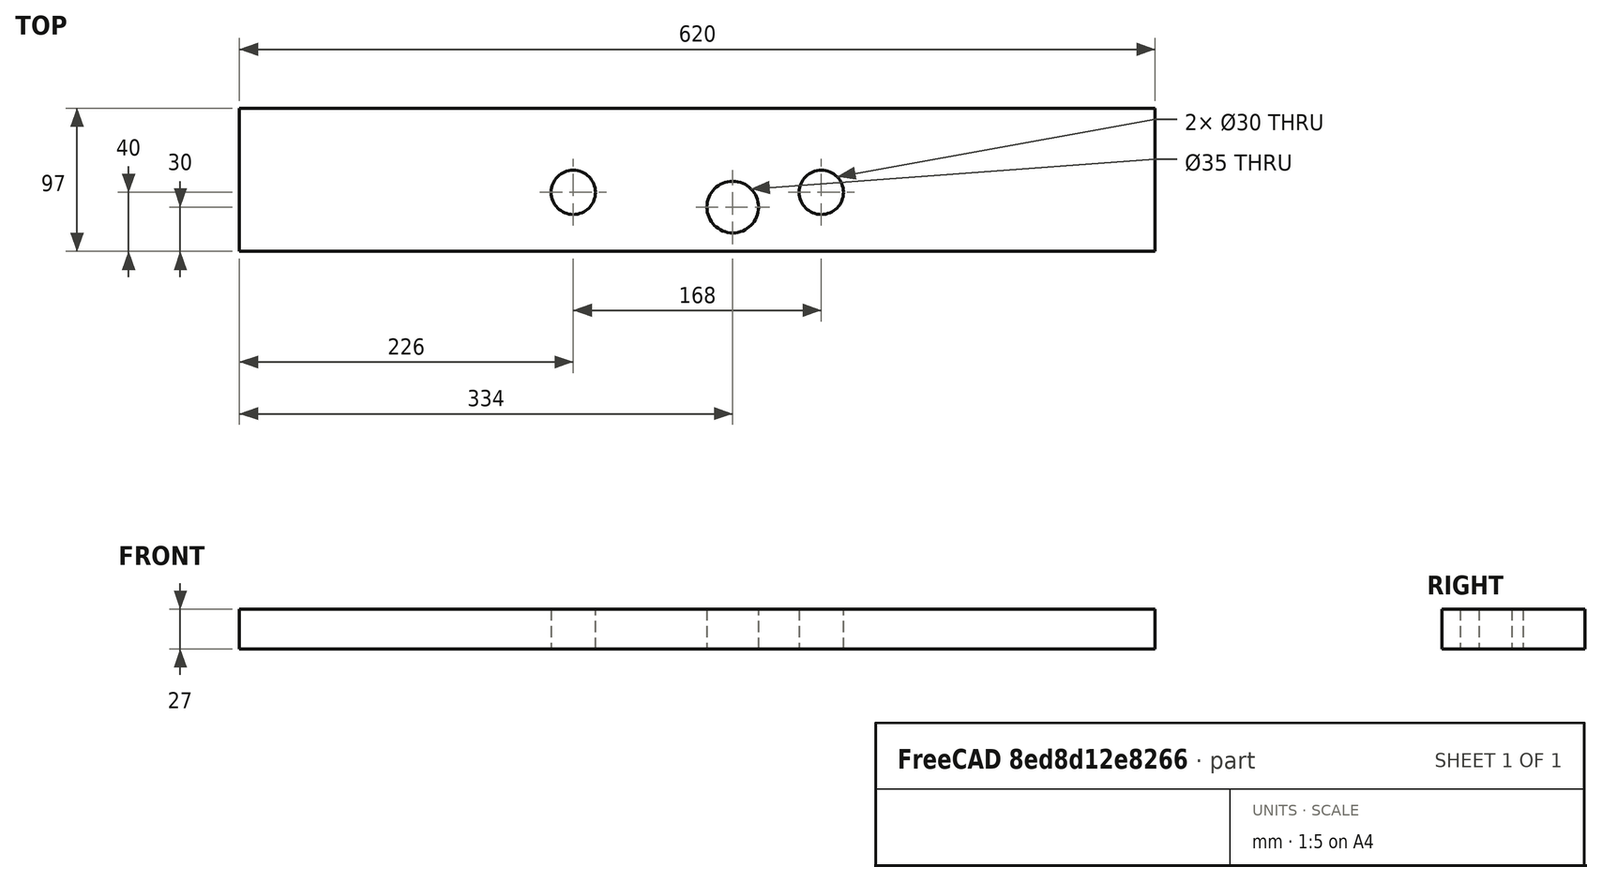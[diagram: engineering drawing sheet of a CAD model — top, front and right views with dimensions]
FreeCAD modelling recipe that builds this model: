
FCSTD DOCUMENT  (FreeCAD 0.20R25131 (Git))
Label: Zange
License: All rights reserved
LicenseURL: http://en.wikipedia.org/wiki/All_rights_reserved
objects: Part::FeaturePython×10, Part::Cylinder×3, App::FeaturePython×2, Part::Box×1, Part::MultiFuse×1, Part::Cut×1
note: 15 computed .brp shape members not serialized (recipe doc carries the construction recipe); baked Part::Feature solids carry a one-line shape summary decoded from their .brp
EXTERNAL_REF file=Grunddaten.FCStd obj=Spreadsheet

FEATURE [Part::Box] Box  label="Cube"
  AttacherType = Attacher::AttachEngine3D
  Height = 27
  Length = 620
  Placement = pos=(-310,0,0) rot=(0,0,1;0rad)
  Width = 97
  expr: .Placement.Base.x = -Length / 2
  expr: Length = <<Grunddaten>>#Spreadsheet.Arbeitsflaeche + 2 * <<Grunddaten>>#Spreadsheet.Ueberstand
  expr: Width = <<Grunddaten>>#Spreadsheet.Hoehe
  expr: Height = <<Grunddaten>>#Spreadsheet.Plattendicke
FEATURE [Part::Cylinder] Cylinder  label="Führung_rechts"
  Angle = 360
  AttacherType = Attacher::AttachEngine3D
  FirstAngle = 0
  Height = 30
  Placement = pos=(84,40,0) rot=(0,0,1;0rad)
  Radius = 15
  SecondAngle = 0
  expr: .Placement.Base.y = -Grunddaten#Spreadsheet.Plattendicke + Grunddaten#Spreadsheet.Hoehe - Grunddaten#Spreadsheet.Spindel_Hoehe
  expr: .Placement.Base.x = Grunddaten#Spreadsheet.Spindel_Links
FEATURE [Part::Cylinder] Cylinder001  label="Führung_links"
  Angle = 360
  AttacherType = Attacher::AttachEngine3D
  FirstAngle = 0
  Height = 30
  Placement = pos=(-84,40,0) rot=(0,0,1;0rad)
  Radius = 15
  SecondAngle = 0
  expr: .Placement.Base.y = -Grunddaten#Spreadsheet.Plattendicke + Grunddaten#Spreadsheet.Hoehe - Grunddaten#Spreadsheet.Spindel_Hoehe
  expr: .Placement.Base.x = -Grunddaten#Spreadsheet.Spindel_Links
FEATURE [Part::Cylinder] Cylinder002  label="Spindel"
  Angle = 360
  AttacherType = Attacher::AttachEngine3D
  FirstAngle = 0
  Height = 30
  Placement = pos=(24,30,0) rot=(0,0,1;0rad)
  Radius = 17.5
  SecondAngle = 0
  expr: .Placement.Base.x = Grunddaten#Spreadsheet.Spindel_Antrieb
  expr: .Placement.Base.y = -Grunddaten#Spreadsheet.Plattendicke + Grunddaten#Spreadsheet.Hoehe - Grunddaten#Spreadsheet.Spindel_Antrieb_Hoehe
FEATURE [App::FeaturePython] Constraints  # WARN: FeaturePython — macro-defined, semantics opaque (R4)
  _Version = 1
FEATURE [Part::MultiFuse] Fusion
  Shapes = -> [Cylinder,Cylinder001,Cylinder002]
FEATURE [Part::Cut] Cut
  Base = -> Box
  Tool = -> Fusion
FEATURE [Part::FeaturePython] Parts  # WARN: FeaturePython — macro-defined, semantics opaque (R4)
  Group = -> [Box,Cylinder,Cylinder001,Cylinder002,Fusion,Cut]
  GroupMode = 0
FEATURE [Part::FeaturePython] Assembly  label="Zange"  # WARN: FeaturePython — macro-defined, semantics opaque (R4)
  AutoRelax = true
  BuildShape = 0
  Freeze = false
  Group = -> [Constraints,Elements,Parts]
  Verbose = false
  _SolverType = 1
  _Version = 1
FEATURE [App::FeaturePython] Elements  # WARN: FeaturePython — macro-defined, semantics opaque (R4)
  Group = -> [Element,Element001,Element002,Element003,Element004,Element005,Element006,Element007]
FEATURE [Part::FeaturePython] Element  label="Vorne"  # link proxy (typed FeaturePython)
  Detach = false
  LinkTransform = true
  LinkedObject = -> Cut [Face3]
  _Parent = -> Elements
FEATURE [Part::FeaturePython] Element001  label="Oben"  # link proxy (typed FeaturePython)
  Detach = false
  LinkTransform = true
  LinkedObject = -> Cut [Face4]
  _Parent = -> Elements
FEATURE [Part::FeaturePython] Element002  label="Spindel"  # link proxy (typed FeaturePython)
  Detach = false
  LinkTransform = true
  LinkedObject = -> Cut [Face7]
  _Parent = -> Elements
FEATURE [Part::FeaturePython] Element003  label="Hinten"  # link proxy (typed FeaturePython)
  Detach = false
  LinkTransform = true
  LinkedObject = -> Cut [Face5]
  _Parent = -> Elements
FEATURE [Part::FeaturePython] Element004  # link proxy (typed FeaturePython)
  Detach = false
  LinkTransform = true
  LinkedObject = -> Cut [Edge10]
  _Parent = -> Elements
FEATURE [Part::FeaturePython] Element005  # link proxy (typed FeaturePython)
  Detach = false
  LinkTransform = true
  LinkedObject = -> Cut [Face6]
  _Parent = -> Elements
FEATURE [Part::FeaturePython] Element006  # link proxy (typed FeaturePython)
  Detach = false
  LinkTransform = true
  LinkedObject = -> Cut [Face2]
  _Parent = -> Elements
FEATURE [Part::FeaturePython] Element007  # link proxy (typed FeaturePython)
  Detach = false
  LinkTransform = true
  LinkedObject = -> Cut [Face1]
  _Parent = -> Elements
